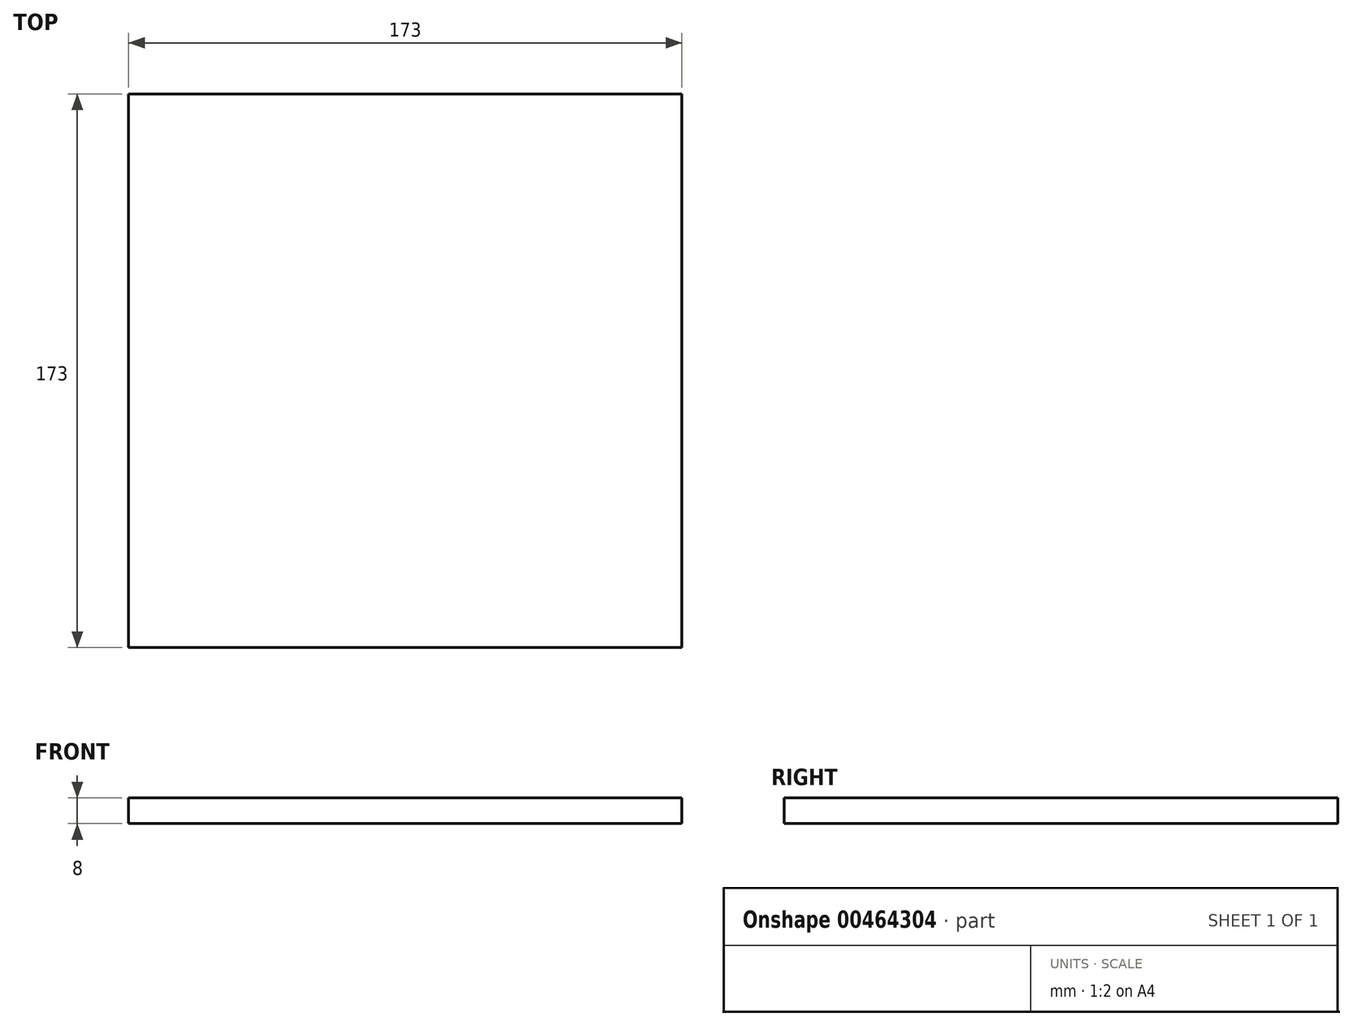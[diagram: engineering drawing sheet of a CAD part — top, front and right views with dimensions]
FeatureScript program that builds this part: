
annotation { "Feature Type Name" : "Feature", "Feature Type Description" : "" }
export const myFeature = defineFeature(function(context is Context, id is Id, definition is map)
    precondition{}
    {
        {
            var Q0;
            Q0=qCreatedBy(makeId("Top.planeOp"),FACE);
            var sketch = newSketch(context, id + "F0", { "sketchPlane" : qUnion([Q0])});
            skLineSegment(sketch, "E0.bottom", {"start": v(-86.5, 86.5) * mm, "end": v(86.5, 86.5) * mm});
            skLineSegment(sketch, "E0.top", {"start": v(-86.5, -86.5) * mm, "end": v(86.5, -86.5) * mm});
            skLineSegment(sketch, "E0.left", {"start": v(-86.5, 86.5) * mm, "end": v(-86.5, -86.5) * mm});
            skLineSegment(sketch, "E0.right", {"start": v(86.5, 86.5) * mm, "end": v(86.5, -86.5) * mm});
            skPoint(sketch, "E0.middle", {"position": v(0, 0) * mm});
            skSolve(sketch);
        }
        {
            var Q0;
            Q0 = qSketchRegion(id + "F0", true);
            extrude(context, id + "F1", {"entities" : qUnion([Q0]), "endBound" : BoundingType.SYMMETRIC, "depth" : 8 * mm});
        }
    });
